# Revit family: Marco - Instrument Storage (BS156) - Copy
name_source: partatom
category: Furniture
units: mm (PartAtom-declared; Revit-internal decimal feet)

## family parameters
Always vertical = Yes
Cut with Voids When Loaded = No
OmniClass Number = 23.40.20.00
OmniClass Title = General Furniture and Specialties
Room Calculation Point = No
Shared = No
Work Plane-Based = No

## types (6) — shared parameters
Depth (calc) = 29.134 "
Height (calc) = 83.976 "
Manufacturer = Marco Group
URL = https://www.madebymarco.net
zero-valued in all types: Default Elevation

## per-type parameters (varying)
| type | Door Type | Model | Shelf Type | Support Beam Width | Width calc |
| BS156-0 | Marco - Instrumental Storage Door : No door | Marco - BS156-0 | Marco - Instrument Storage Shelf | 27.666 " | 27.441 " |
| BS156-3 | Marco - Instrumental Storage Door : Marco - Individual wood door | Marco - BS156-3 | Marco - Instrument Storage Shelf | 27.666 " | 27.441 " |
| BS156-4 | Marco - Instrumental Storage Door : Marco - Individual steel door | Marco - BS156-4 | Marco - Instrument Storage Shelf | 27.666 " | 27.441 " |
| BS156N-0 | Marco - Instrumental Storage Door : No door | Marco - BS156N-0 | Marco - Instrument Storage Shelf : Marco - Instrument Storage Shelf N type | 21.666 " | 21.441 " |
| BS156N-3 | Marco - Instrumental Storage Door : Marco - Individual wood door N | Marco - BS156N-3 | Marco - Instrument Storage Shelf : Marco - Instrument Storage Shelf N type | 21.666 " | 21.441 " |
| BS156N-4 | Marco - Instrumental Storage Door : Marco - Individual steel door N | Marco - BS156N-4 | Marco - Instrument Storage Shelf : Marco - Instrument Storage Shelf N type | 21.666 " | 21.441 " |

## geometry (parser evidence)
native form markers: Sweep x16
no freeform markers — native parametric forms only
